# Revit family: ledspotra_hq2_8w-dim-4000-40d-wh-ip44_140061283
name_source: partatom
category: Leuchten
revit_build: Autodesk Revit 2016 (Build: 20190508_0715(x64)
units: mm (PartAtom-declared; Revit-internal decimal feet)

## family parameters
Basisbauteil = Fläche
Beim Laden mit Abzugskörper schneiden = Nein
Bemaßung runder Anschluss = Durchmesser verwenden
Gemeinsam genutzt = Nein
Lichtquelle = Nein
Raumberechnungspunkt = Nein
Teiletyp = Normal

## types (1)
- LEDSpotRA HQ2 8W-Dim-4000-40D-WH-IP44 (1 x LED, 680 lm)
    Approval mark = CE, ENEC
    Beschreibung = Attractive tiltable recessed spotlight with comfortable light beam. Up to 85% lower energy consumption than halogen spotlights. Unique light mixing technique and optics design, UGR16. Good beam orientation adjustment, providing great flexibility.
    CIE Flux Codes = 97 99 100 100 100
    Control Gear = Electronic ballast
    Height = 0 mm  [stored 0 ft]
    Hersteller = OPPLE
    Lamp Light Flux = 680 lm
    Lamp count = 1
    Lampe = 1 x LED
    Length = 90 mm
    Luminous efficacy = 85 lm/W
    ModVariant = Nein
    Modell = 140061283
    Mounting Place = Ceiling
    Mounting Type = Recessed
    Number of Poles = 1
    OnlyDefault = Ja
    Power Factor = 1
    Product Name = LEDSpotRA HQ2 8W-Dim-4000-40D-WH-IP44
    Product group = Spot Round Adjustable HQ
    ProductGroupID = 424
    Protection Class = Protection class II
    Protection Degree = IP 44
    RLX_Detail_Level = 1
    RlxData = <blob elided: 137101 chars, md5=a5a1b4e4>
    Scheinlast = 8 VA
    Socket = socket
    Standby Power = 0 W
    System Light Flux = 679 lm
    System Power = 8 W
    Typenbild = 140061283.jpg
    Typenkommentare = Product without accessories
    URL = http://relux.com
    VarID = ---
    Voltage = 0 V
    Vorgabe-Ansicht = 1800 mm
    Weight = 0.00 kg
    Width = 0 mm  [stored 0 ft]

note: [stored X ft] marks values corroborated as IEEE doubles in the binary element streams (Revit-internal decimal feet)

## geometry (parser evidence)
native form markers: Sweep x11
no freeform markers — native parametric forms only
